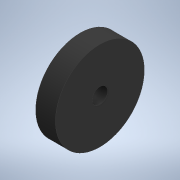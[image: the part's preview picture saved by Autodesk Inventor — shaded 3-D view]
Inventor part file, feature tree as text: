
AUTODESK INVENTOR PART (.ipt)
format: ipt  version: 2020 (Build 240168000, 168)  size: 95,744 bytes
history: native  units: in
note: dims shown in document units (in); Inventor stores cm internally (conversion verified against a paired STEP export)
features: extrude x1, sketch x1
ambient origin geometry x8: Origin, YZ Plane, XZ Plane, XY Plane, X Axis, Y Axis, Z Axis, Center Point
bodies: Solid1 (feature_tree)
feature tree (2):
  extrude  "Extrusion1"  Depth=0.5in
  sketch  "Sketch1"  dims[d0=0.3937in d1=2.25in d2=0.5in d3=0.0in]
